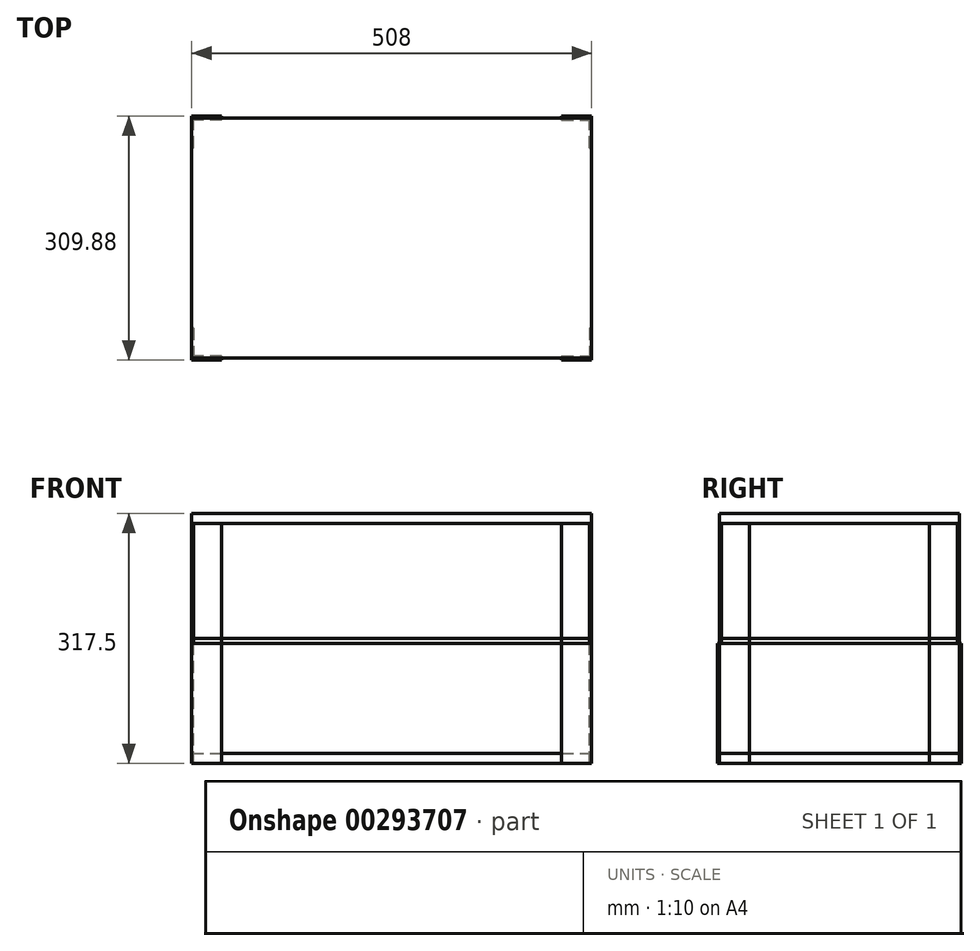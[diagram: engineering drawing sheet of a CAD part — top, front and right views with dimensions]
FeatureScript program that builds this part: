
annotation { "Feature Type Name" : "Feature", "Feature Type Description" : "" }
export const myFeature = defineFeature(function(context is Context, id is Id, definition is map)
    precondition{}
    {
        {
            var Q0;
            Q0=qCreatedBy(makeId("Top.planeOp"),FACE);
            var sketch = newSketch(context, id + "F0", { "sketchPlane" : qUnion([Q0])});
            skLineSegment(sketch, "E0.bottom", {"start": v(-254, 152.4) * mm, "end": v(254, 152.4) * mm});
            skLineSegment(sketch, "E0.top", {"start": v(-254, -152.4) * mm, "end": v(254, -152.4) * mm});
            skLineSegment(sketch, "E0.left", {"start": v(-254, 152.4) * mm, "end": v(-254, -152.4) * mm});
            skLineSegment(sketch, "E0.right", {"start": v(254, 152.4) * mm, "end": v(254, -152.4) * mm});
            skPoint(sketch, "E0.middle", {"position": v(0, 0) * mm});
            skSolve(sketch);
        }
        {
            var Q0;
            Q0 = qSketchRegion(id + "F0", true);
            extrude(context, id + "F1", {"entities" : qUnion([Q0]), "depth" : 12.7 * mm});
        }
        {
            var Q0;
            Q0=qCreatedBy(makeId("Front.planeOp"),FACE);
            var sketch = newSketch(context, id + "F2", { "sketchPlane" : qUnion([Q0])});
            skLineSegment(sketch, "E1", {"start": v(0, 0) * mm, "end": v(0, 152.4) * mm});
            skLineSegment(sketch, "E2", {"start": v(0, 152.4) * mm, "end": v(38.1, 152.4) * mm});
            skLineSegment(sketch, "E3", {"start": v(38.1, 152.4) * mm, "end": v(38.1, 0) * mm});
            skLineSegment(sketch, "E4", {"start": v(38.1, 0) * mm, "end": v(0, 0) * mm});
            skSolve(sketch);
        }
        {
            var Q0;
            Q0=qCreatedBy(makeId("Right.planeOp"),FACE);
            var sketch = newSketch(context, id + "F3", { "sketchPlane" : qUnion([Q0])});
            skLineSegment(sketch, "E5.0", {"start": v(0, 0) * mm, "end": v(0, 152.4) * mm});
            skLineSegment(sketch, "E6", {"start": v(0, 152.4) * mm, "end": v(38.1, 152.4) * mm});
            skLineSegment(sketch, "E7", {"start": v(38.1, 152.4) * mm, "end": v(38.1, 0) * mm});
            skLineSegment(sketch, "E8", {"start": v(38.1, 0) * mm, "end": v(0, 0) * mm});
            skSolve(sketch);
        }
        {
            var Q0;
            Q0=makeQuery(id+"F2.imprint","IMPRINT",FACE,{"disambiguationData":[TD([[makeQuery(id+"F2.imprint","IMPRINT",EDGE,{"derivedFrom":sQuery(id+"F2.wireOp",EDGE,"E1")}),-1.0]])]});
            extrude(context, id + "F4", {"entities" : qUnion([Q0]), "depth" : 2.54 * mm});
        }
        {
            var Q0;
            Q0=makeQuery(id+"F3.imprint","IMPRINT",FACE,{"disambiguationData":[TD([[makeQuery(id+"F3.imprint","IMPRINT",EDGE,{"derivedFrom":sQuery(id+"F3.wireOp",EDGE,"E5.0")}),-1.0]])]});
            extrude(context, id + "F5", {"entities" : qUnion([Q0]), "depth" : 2.54 * mm});
        }
        {
            var Q0;
            Q0=makeQuery(id+"F4.opExtrude","SWEPT_BODY",BODY,{"disambiguationData":[OSD([sQuery(id+"F2.wireOp",EDGE,"E1"),sQuery(id+"F2.wireOp",EDGE,"E2"),sQuery(id+"F2.wireOp",EDGE,"E3"),sQuery(id+"F2.wireOp",EDGE,"E4")])]});
            var Q1;
            Q1=makeQuery(id+"F5.opExtrude","SWEPT_BODY",BODY,{"disambiguationData":[OSD([sQuery(id+"F3.wireOp",EDGE,"E5.0"),sQuery(id+"F3.wireOp",EDGE,"E6"),sQuery(id+"F3.wireOp",EDGE,"E7"),sQuery(id+"F3.wireOp",EDGE,"E8")])]});
            transform(context, id + "F6", {"entities" : qUnion([Q0, Q1]), "transformType" : TransformType.TRANSLATION_3D, "dx" : -254 * mm, "dy" : -152.4 * mm, "dz" : 0 * mm, "makeCopy" : false});
        }
        {
            var Q0;
            Q0=makeQuery(id+"F5.opExtrude","SWEPT_BODY",BODY,{"disambiguationData":[OSD([sQuery(id+"F3.wireOp",EDGE,"E5.0"),sQuery(id+"F3.wireOp",EDGE,"E6"),sQuery(id+"F3.wireOp",EDGE,"E7"),sQuery(id+"F3.wireOp",EDGE,"E8")])]});
            var Q1;
            Q1=makeQuery(id+"F4.opExtrude","SWEPT_BODY",BODY,{"disambiguationData":[OSD([sQuery(id+"F2.wireOp",EDGE,"E1"),sQuery(id+"F2.wireOp",EDGE,"E2"),sQuery(id+"F2.wireOp",EDGE,"E3"),sQuery(id+"F2.wireOp",EDGE,"E4")])]});
            var Q2;
            Q2=qCreatedBy(makeId("Right.planeOp"),FACE);
            mirror(context, id + "F7", {"entities" : qUnion([Q0, Q1]), "mirrorPlane" : qUnion([Q2])});
        }
        {
            var Q0;
            Q0=makeQuery(id+"F7.opPattern","COPY",BODY,{"derivedFrom":makeQuery(id+"F5.opExtrude","SWEPT_BODY",BODY,{"disambiguationData":[OSD([sQuery(id+"F3.wireOp",EDGE,"E5.0"),sQuery(id+"F3.wireOp",EDGE,"E6"),sQuery(id+"F3.wireOp",EDGE,"E7"),sQuery(id+"F3.wireOp",EDGE,"E8")])]}),"instanceName":"1"});
            var Q1;
            Q1=makeQuery(id+"F7.opPattern","COPY",BODY,{"derivedFrom":makeQuery(id+"F4.opExtrude","SWEPT_BODY",BODY,{"disambiguationData":[OSD([sQuery(id+"F2.wireOp",EDGE,"E1"),sQuery(id+"F2.wireOp",EDGE,"E2"),sQuery(id+"F2.wireOp",EDGE,"E3"),sQuery(id+"F2.wireOp",EDGE,"E4")])]}),"instanceName":"1"});
            var Q2;
            Q2=makeQuery(id+"F5.opExtrude","SWEPT_BODY",BODY,{"disambiguationData":[OSD([sQuery(id+"F3.wireOp",EDGE,"E5.0"),sQuery(id+"F3.wireOp",EDGE,"E6"),sQuery(id+"F3.wireOp",EDGE,"E7"),sQuery(id+"F3.wireOp",EDGE,"E8")])]});
            var Q3;
            Q3=makeQuery(id+"F4.opExtrude","SWEPT_BODY",BODY,{"disambiguationData":[OSD([sQuery(id+"F2.wireOp",EDGE,"E1"),sQuery(id+"F2.wireOp",EDGE,"E2"),sQuery(id+"F2.wireOp",EDGE,"E3"),sQuery(id+"F2.wireOp",EDGE,"E4")])]});
            var Q4;
            Q4=qCreatedBy(makeId("Front.planeOp"),FACE);
            mirror(context, id + "F8", {"entities" : qUnion([Q0, Q1, Q2, Q3]), "mirrorPlane" : qUnion([Q4])});
        }
        {
            var Q0;
            Q0=makeQuery(id+"F8.opPattern","COPY",FACE,{"derivedFrom":makeQuery(id+"F7.opPattern","COPY",FACE,{"derivedFrom":makeQuery(id+"F4.opExtrude","SWEPT_FACE",FACE,{"disambiguationData":[OSD([sQuery(id+"F2.wireOp",EDGE,"E2")])]}),"instanceName":"1"}),"instanceName":"1"});
            var sketch = newSketch(context, id + "F9", { "sketchPlane" : qUnion([Q0])});
            skLineSegment(sketch, "E9.bottom", {"start": v(254, -152.4) * mm, "end": v(-254, -152.4) * mm});
            skLineSegment(sketch, "E9.top", {"start": v(254, 152.4) * mm, "end": v(-254, 152.4) * mm});
            skLineSegment(sketch, "E9.left", {"start": v(254, -152.4) * mm, "end": v(254, 152.4) * mm});
            skLineSegment(sketch, "E9.right", {"start": v(-254, -152.4) * mm, "end": v(-254, 152.4) * mm});
            skPoint(sketch, "E9.middle", {"position": v(0, 0) * mm});
            skSolve(sketch);
        }
        {
            var Q0;
            Q0 = qSketchRegion(id + "F9", true);
            extrude(context, id + "F10", {"entities" : qUnion([Q0]), "depth" : 6.35 * mm});
        }
        {
            var Q0;
            Q0=makeQuery(id+"F7.opPattern","COPY",BODY,{"derivedFrom":makeQuery(id+"F5.opExtrude","SWEPT_BODY",BODY,{"disambiguationData":[OSD([sQuery(id+"F3.wireOp",EDGE,"E5.0"),sQuery(id+"F3.wireOp",EDGE,"E6"),sQuery(id+"F3.wireOp",EDGE,"E7"),sQuery(id+"F3.wireOp",EDGE,"E8")])]}),"instanceName":"1"});
            var Q1;
            Q1=makeQuery(id+"F10.opExtrude","CAP_FACE",FACE,{"disambiguationData":[OSD([sQuery(id+"F9.wireOp",EDGE,"E9.bottom"),sQuery(id+"F9.wireOp",EDGE,"E9.top"),sQuery(id+"F9.wireOp",EDGE,"E9.left"),sQuery(id+"F9.wireOp",EDGE,"E9.right")])],"isStart":true});
            mirror(context, id + "F11", {"entities" : qUnion([Q0]), "mirrorPlane" : qUnion([Q1])});
        }
        {
            var Q0;
            Q0=makeQuery(id+"F11.opPattern","COPY",BODY,{"derivedFrom":makeQuery(id+"F7.opPattern","COPY",BODY,{"derivedFrom":makeQuery(id+"F5.opExtrude","SWEPT_BODY",BODY,{"disambiguationData":[OSD([sQuery(id+"F3.wireOp",EDGE,"E5.0"),sQuery(id+"F3.wireOp",EDGE,"E6"),sQuery(id+"F3.wireOp",EDGE,"E7"),sQuery(id+"F3.wireOp",EDGE,"E8")])]}),"instanceName":"1"}),"instanceName":"1"});
            var Q1;
            Q1=makeQuery(id+"F10.opExtrude","SWEPT_FACE",FACE,{"disambiguationData":[OSD([sQuery(id+"F9.wireOp",EDGE,"E9.bottom")])]});
            mirror(context, id + "F12", {"entities" : qUnion([Q0]), "mirrorPlane" : qUnion([Q1])});
        }
        {
            var Q0;
            Q0=makeQuery(id+"F7.opPattern","COPY",EDGE,{"derivedFrom":makeQuery(id+"F4.opExtrude","CAP_EDGE",EDGE,{"disambiguationData":[OSD([sQuery(id+"F2.wireOp",EDGE,"E2")])],"isStart":false}),"instanceName":"1"});
            cPoint(context, id + "F13", {"entities" : qUnion([Q0]), "parameter" : 0.5});
        }
        {
            var Q0;
            Q0=makeQuery(id+"F12.opPattern","COPY",BODY,{"derivedFrom":makeQuery(id+"F11.opPattern","COPY",BODY,{"derivedFrom":makeQuery(id+"F7.opPattern","COPY",BODY,{"derivedFrom":makeQuery(id+"F5.opExtrude","SWEPT_BODY",BODY,{"disambiguationData":[OSD([sQuery(id+"F3.wireOp",EDGE,"E5.0"),sQuery(id+"F3.wireOp",EDGE,"E6"),sQuery(id+"F3.wireOp",EDGE,"E7"),sQuery(id+"F3.wireOp",EDGE,"E8")])]}),"instanceName":"1"}),"instanceName":"1"}),"instanceName":"1"});
            var Q1;
            Q1=makeQuery(id+"F7.opPattern","COPY",VERTEX,{"derivedFrom":makeQuery(id+"F5.opExtrude","CAP_VERTEX",VERTEX,{"disambiguationData":[OSD([sQuery(id+"F3.wireOp",EDGE,"E5.0"),sQuery(id+"F3.wireOp",EDGE,"E6")])],"isStart":false}),"instanceName":"1"});
            var Q2;
            Q2 = qCreatedBy(id + "F13" ,VERTEX);
            var Q3;
            Q3=makeQuery(id+"F11.opPattern","COPY",EDGE,{"derivedFrom":makeQuery(id+"F7.opPattern","COPY",EDGE,{"derivedFrom":makeQuery(id+"F5.opExtrude","CAP_EDGE",EDGE,{"disambiguationData":[OSD([sQuery(id+"F3.wireOp",EDGE,"E5.0")])],"isStart":true}),"instanceName":"1"}),"instanceName":"1"});
            transform(context, id + "F14", {"entities" : qUnion([Q0]), "transformType" : TransformType.ROTATION, "transformAxis" : qUnion([Q3]), "angle" : 90 * degree, "makeCopy" : false});
        }
        {
            var Q0;
            Q0=makeQuery(id+"F11.opPattern","COPY",BODY,{"derivedFrom":makeQuery(id+"F7.opPattern","COPY",BODY,{"derivedFrom":makeQuery(id+"F5.opExtrude","SWEPT_BODY",BODY,{"disambiguationData":[OSD([sQuery(id+"F3.wireOp",EDGE,"E5.0"),sQuery(id+"F3.wireOp",EDGE,"E6"),sQuery(id+"F3.wireOp",EDGE,"E7"),sQuery(id+"F3.wireOp",EDGE,"E8")])]}),"instanceName":"1"}),"instanceName":"1"});
            var Q1;
            Q1=makeQuery(id+"F12.opPattern","COPY",BODY,{"derivedFrom":makeQuery(id+"F11.opPattern","COPY",BODY,{"derivedFrom":makeQuery(id+"F7.opPattern","COPY",BODY,{"derivedFrom":makeQuery(id+"F5.opExtrude","SWEPT_BODY",BODY,{"disambiguationData":[OSD([sQuery(id+"F3.wireOp",EDGE,"E5.0"),sQuery(id+"F3.wireOp",EDGE,"E6"),sQuery(id+"F3.wireOp",EDGE,"E7"),sQuery(id+"F3.wireOp",EDGE,"E8")])]}),"instanceName":"1"}),"instanceName":"1"}),"instanceName":"1"});
            var Q2;
            Q2=qCreatedBy(makeId("Front.planeOp"),FACE);
            mirror(context, id + "F15", {"entities" : qUnion([Q0, Q1]), "mirrorPlane" : qUnion([Q2])});
        }
        {
            var Q0;
            Q0=makeQuery(id+"F15.opPattern","COPY",BODY,{"derivedFrom":makeQuery(id+"F11.opPattern","COPY",BODY,{"derivedFrom":makeQuery(id+"F7.opPattern","COPY",BODY,{"derivedFrom":makeQuery(id+"F5.opExtrude","SWEPT_BODY",BODY,{"disambiguationData":[OSD([sQuery(id+"F3.wireOp",EDGE,"E5.0"),sQuery(id+"F3.wireOp",EDGE,"E6"),sQuery(id+"F3.wireOp",EDGE,"E7"),sQuery(id+"F3.wireOp",EDGE,"E8")])]}),"instanceName":"1"}),"instanceName":"1"}),"instanceName":"1"});
            var Q1;
            Q1=makeQuery(id+"F15.opPattern","COPY",BODY,{"derivedFrom":makeQuery(id+"F12.opPattern","COPY",BODY,{"derivedFrom":makeQuery(id+"F11.opPattern","COPY",BODY,{"derivedFrom":makeQuery(id+"F7.opPattern","COPY",BODY,{"derivedFrom":makeQuery(id+"F5.opExtrude","SWEPT_BODY",BODY,{"disambiguationData":[OSD([sQuery(id+"F3.wireOp",EDGE,"E5.0"),sQuery(id+"F3.wireOp",EDGE,"E6"),sQuery(id+"F3.wireOp",EDGE,"E7"),sQuery(id+"F3.wireOp",EDGE,"E8")])]}),"instanceName":"1"}),"instanceName":"1"}),"instanceName":"1"}),"instanceName":"1"});
            var Q2;
            Q2=makeQuery(id+"F12.opPattern","COPY",BODY,{"derivedFrom":makeQuery(id+"F11.opPattern","COPY",BODY,{"derivedFrom":makeQuery(id+"F7.opPattern","COPY",BODY,{"derivedFrom":makeQuery(id+"F5.opExtrude","SWEPT_BODY",BODY,{"disambiguationData":[OSD([sQuery(id+"F3.wireOp",EDGE,"E5.0"),sQuery(id+"F3.wireOp",EDGE,"E6"),sQuery(id+"F3.wireOp",EDGE,"E7"),sQuery(id+"F3.wireOp",EDGE,"E8")])]}),"instanceName":"1"}),"instanceName":"1"}),"instanceName":"1"});
            var Q3;
            Q3=makeQuery(id+"F11.opPattern","COPY",BODY,{"derivedFrom":makeQuery(id+"F7.opPattern","COPY",BODY,{"derivedFrom":makeQuery(id+"F5.opExtrude","SWEPT_BODY",BODY,{"disambiguationData":[OSD([sQuery(id+"F3.wireOp",EDGE,"E5.0"),sQuery(id+"F3.wireOp",EDGE,"E6"),sQuery(id+"F3.wireOp",EDGE,"E7"),sQuery(id+"F3.wireOp",EDGE,"E8")])]}),"instanceName":"1"}),"instanceName":"1"});
            var Q4;
            Q4=qCreatedBy(makeId("Right.planeOp"),FACE);
            mirror(context, id + "F16", {"entities" : qUnion([Q0, Q1, Q2, Q3]), "mirrorPlane" : qUnion([Q4])});
        }
        {
            var Q0;
            Q0=makeQuery(id+"F1.opExtrude","SWEPT_BODY",BODY,{"disambiguationData":[OSD([sQuery(id+"F0.wireOp",EDGE,"E0.bottom"),sQuery(id+"F0.wireOp",EDGE,"E0.top"),sQuery(id+"F0.wireOp",EDGE,"E0.left"),sQuery(id+"F0.wireOp",EDGE,"E0.right")])]});
            var Q1;
            Q1=makeQuery(id+"F10.opExtrude","CAP_FACE",FACE,{"disambiguationData":[OSD([sQuery(id+"F9.wireOp",EDGE,"E9.bottom"),sQuery(id+"F9.wireOp",EDGE,"E9.top"),sQuery(id+"F9.wireOp",EDGE,"E9.left"),sQuery(id+"F9.wireOp",EDGE,"E9.right")])],"isStart":false});
            mirror(context, id + "F17", {"entities" : qUnion([Q0]), "mirrorPlane" : qUnion([Q1])});
        }
    });
